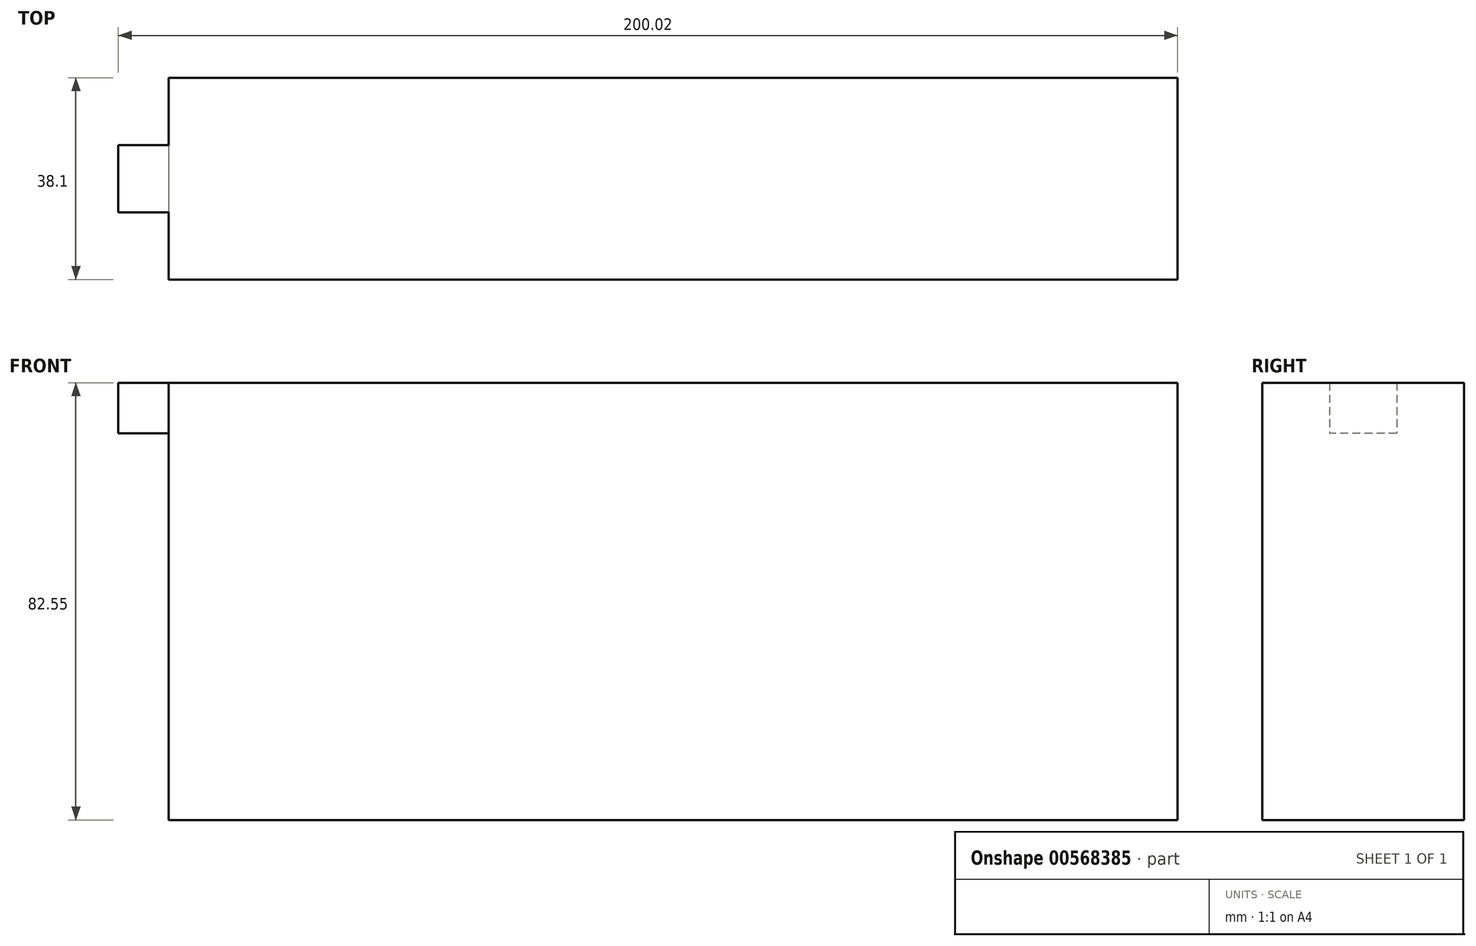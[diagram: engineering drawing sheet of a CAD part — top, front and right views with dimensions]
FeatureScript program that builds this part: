
annotation { "Feature Type Name" : "Feature", "Feature Type Description" : "" }
export const myFeature = defineFeature(function(context is Context, id is Id, definition is map)
    precondition{}
    {
        {
            var Q0;
            Q0=qCreatedBy(makeId("Top.planeOp"),FACE);
            var sketch = newSketch(context, id + "F0", { "sketchPlane" : qUnion([Q0])});
            skLineSegment(sketch, "E0.bottom", {"start": v(-149.93, 9.69) * mm, "end": v(40.57, 9.69) * mm});
            skLineSegment(sketch, "E0.top", {"start": v(-149.93, -28.41) * mm, "end": v(40.57, -28.41) * mm});
            skLineSegment(sketch, "E0.left", {"start": v(-149.93, 9.69) * mm, "end": v(-149.93, -28.41) * mm});
            skLineSegment(sketch, "E0.right", {"start": v(40.57, 9.69) * mm, "end": v(40.57, -28.41) * mm});
            skSolve(sketch);
        }
        {
            var Q0;
            Q0=makeQuery(id+"F0.imprint","IMPRINT",FACE,{"disambiguationData":[TD([[makeQuery(id+"F0.imprint","IMPRINT",EDGE,{"derivedFrom":sQuery(id+"F0.wireOp",EDGE,"E0.bottom")}),-1.0]])]});
            extrude(context, id + "F1", {"entities" : qUnion([Q0]), "depth" : 82.55 * mm, "offsetDistance" : 25.4 * mm});
        }
        {
            var Q0;
            Q0=makeQuery(id+"F1.opExtrude","SWEPT_FACE",FACE,{"disambiguationData":[OSD([sQuery(id+"F0.wireOp",EDGE,"E0.left")])]});
            var sketch = newSketch(context, id + "F2", { "sketchPlane" : qUnion([Q0])});
            skLineSegment(sketch, "E1.bottom", {"start": v(3.01, 82.55) * mm, "end": v(15.71, 82.55) * mm});
            skLineSegment(sketch, "E1.top", {"start": v(3.01, 73.03) * mm, "end": v(15.71, 73.03) * mm});
            skLineSegment(sketch, "E1.left", {"start": v(3.01, 82.55) * mm, "end": v(3.01, 73.03) * mm});
            skLineSegment(sketch, "E1.right", {"start": v(15.71, 82.55) * mm, "end": v(15.71, 73.03) * mm});
            skSolve(sketch);
        }
        {
            var Q0;
            Q0 = qSketchRegion(id + "F2", true);
            extrude(context, id + "F3", {"entities" : qUnion([Q0]), "operationType" : NewBodyOperationType.ADD, "depth" : 9.52 * mm, "offsetDistance" : 25.4 * mm});
        }
    });
